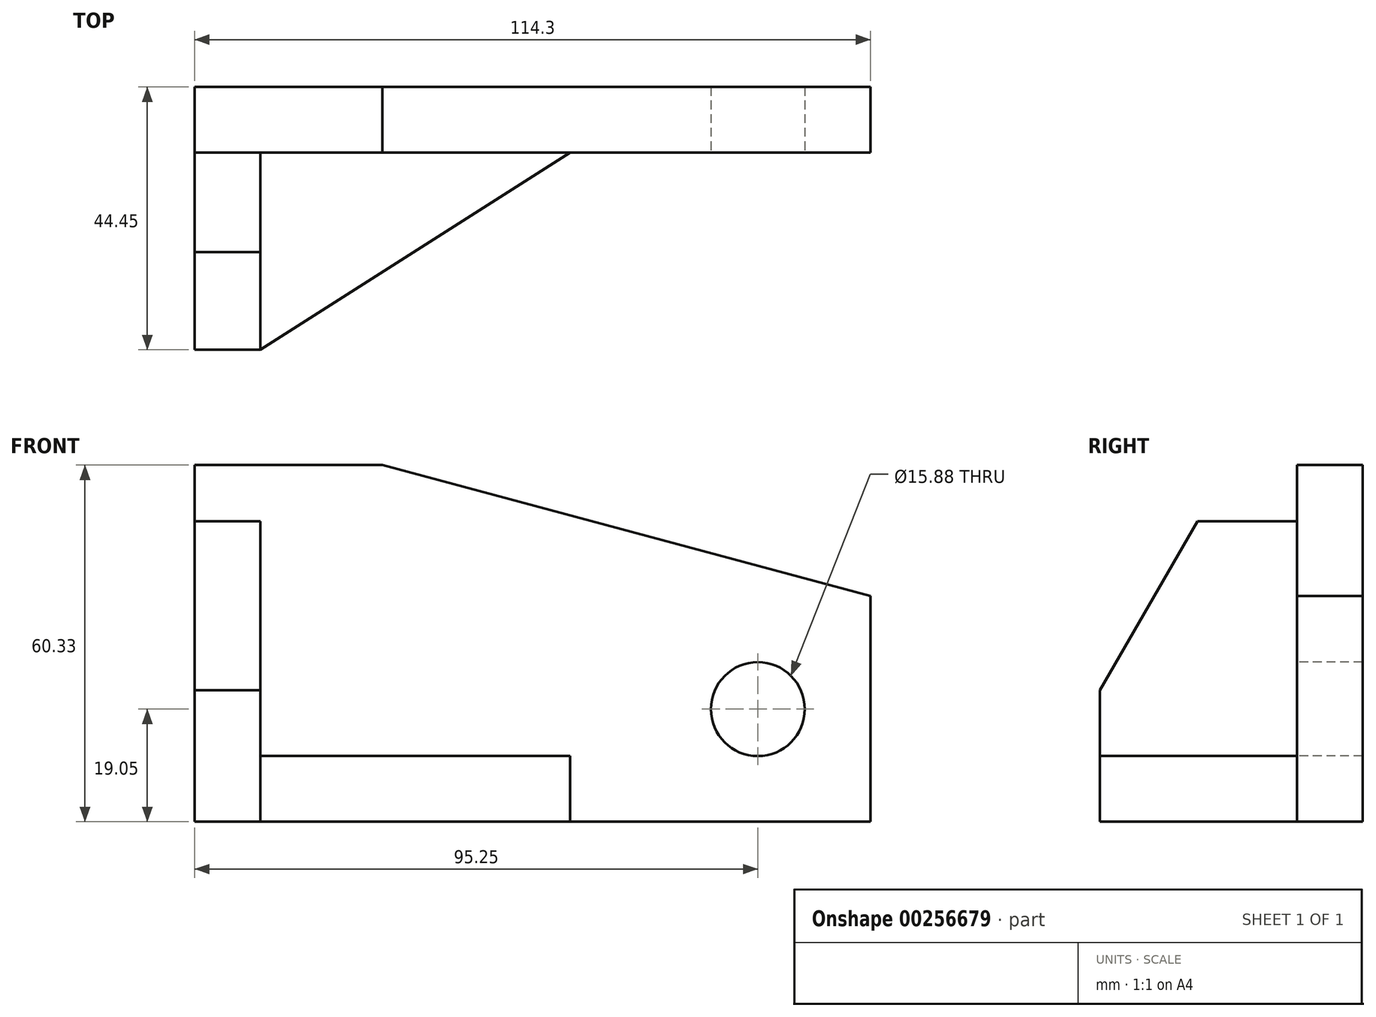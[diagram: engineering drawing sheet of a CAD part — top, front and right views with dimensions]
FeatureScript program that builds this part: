
annotation { "Feature Type Name" : "Feature", "Feature Type Description" : "" }
export const myFeature = defineFeature(function(context is Context, id is Id, definition is map)
    precondition{}
    {
        {
            var Q0;
            Q0=qCreatedBy(makeId("Top.planeOp"),FACE);
            var sketch = newSketch(context, id + "F0", { "sketchPlane" : qUnion([Q0])});
            skLineSegment(sketch, "E0", {"start": v(0, 0) * mm, "end": v(114.3, 0) * mm});
            skLineSegment(sketch, "E1", {"start": v(114.3, 0) * mm, "end": v(114.3, -11.11) * mm});
            skLineSegment(sketch, "E2", {"start": v(0, 0) * mm, "end": v(0, -44.45) * mm});
            skLineSegment(sketch, "E3", {"start": v(0, -44.45) * mm, "end": v(11.11, -44.45) * mm});
            skLineSegment(sketch, "E4", {"start": v(11.11, -44.45) * mm, "end": v(11.11, -11.11) * mm});
            skLineSegment(sketch, "E5", {"start": v(11.11, -11.11) * mm, "end": v(114.3, -11.11) * mm});
            skLineSegment(sketch, "E6", {"start": v(11.11, -44.45) * mm, "end": v(63.5, -11.11) * mm});
            skLineSegment(sketch, "E7", {"start": v(11.11, -11.11) * mm, "end": v(0, -11.11) * mm});
            skLineSegment(sketch, "E8", {"start": v(11.11, -44.45) * mm, "end": v(0, -44.45) * mm});
            skSolve(sketch);
        }
        {
            var Q0;
            {var subQ4=sQuery(id+"F0.wireOp",EDGE,"E0");Q0=makeQuery(id+"F0.imprint","IMPRINT",FACE,{"disambiguationData":[TD([[makeQuery(id+"F0.imprint","IMPRINT",EDGE,{"derivedFrom":subQ4}),-1.0]])]});}
            extrude(context, id + "F1", {"entities" : qUnion([Q0]), "depth" : 60.32 * mm});
        }
        {
            var Q0;
            {var subQ0=sQuery(id+"F0.wireOp",EDGE,"E4");Q0=makeQuery(id+"F0.imprint","IMPRINT",FACE,{"disambiguationData":[TD([[makeQuery(id+"F0.imprint","IMPRINT",EDGE,{"derivedFrom":subQ0}),-1.0]])]});}
            extrude(context, id + "F2", {"entities" : qUnion([Q0]), "operationType" : NewBodyOperationType.ADD, "depth" : 11.1 * mm});
        }
        {
            var Q0;
            Q0=makeQuery(id+"F1.opExtrude","SWEPT_FACE",FACE,{"disambiguationData":[OSD([sQuery(id+"F0.wireOp",EDGE,"E5"),sQuery(id+"F0.wireOp",EDGE,"E7")])]});
            var sketch = newSketch(context, id + "F3", { "sketchPlane" : qUnion([Q0])});
            skLineSegment(sketch, "E9", {"start": v(0, 60.33) * mm, "end": v(31.75, 60.33) * mm});
            skLineSegment(sketch, "E10", {"start": v(31.75, 60.33) * mm, "end": v(114.3, 38.2) * mm});
            skLineSegment(sketch, "E11", {"start": v(114.3, 0) * mm, "end": v(95.25, 0) * mm});
            skLineSegment(sketch, "E12", {"start": v(95.25, 0) * mm, "end": v(95.25, 19.05) * mm});
            skCircle(sketch, "E13", {"center": v(95.25, 19.05) * mm, "radius": 7.94 * mm});
            skSolve(sketch);
        }
        {
            var Q0;
            {var subQ0=sQuery(id+"F3.wireOp",EDGE,"E10");Q0=makeQuery(id+"F3.imprint","IMPRINT",FACE,{"disambiguationData":[TD([[makeQuery(id+"F3.imprint","IMPRINT",EDGE,{"derivedFrom":subQ0}),1.0]])]});}
            extrude(context, id + "F4", {"entities" : qUnion([Q0]), "operationType" : NewBodyOperationType.REMOVE, "oppositeDirection" : true, "depth" : 11.1 * mm});
        }
        {
            var Q0;
            Q0=makeQuery(id+"F0.imprint","IMPRINT",FACE,{"disambiguationData":[TD([[makeQuery(id+"F0.imprint","IMPRINT",EDGE,{"derivedFrom":sQuery(id+"F0.wireOp",EDGE,"E4")}),1.0]])]});
            extrude(context, id + "F5", {"entities" : qUnion([Q0]), "operationType" : NewBodyOperationType.ADD, "depth" : 50.8 * mm});
        }
        {
            var Q0;
            Q0=makeQuery(id+"F3.imprint","IMPRINT",FACE,{"disambiguationData":[TD([[makeQuery(id+"F3.imprint","IMPRINT",EDGE,{"derivedFrom":sQuery(id+"F3.wireOp",EDGE,"E13")}),1.0]])]});
            extrude(context, id + "F6", {"entities" : qUnion([Q0]), "operationType" : NewBodyOperationType.REMOVE, "oppositeDirection" : true, "depth" : 25.4 * mm});
        }
        {
            var Q0;
            Q0=makeQuery(id+"F5.opExtrude","SWEPT_FACE",FACE,{"disambiguationData":[OSD([sQuery(id+"F0.wireOp",EDGE,"E4")])]});
            var sketch = newSketch(context, id + "F7", { "sketchPlane" : qUnion([Q0])});
            skLineSegment(sketch, "E14", {"start": v(-44.45, 0) * mm, "end": v(-44.45, 22.23) * mm});
            skLineSegment(sketch, "E15", {"start": v(-44.45, 22.23) * mm, "end": v(-27.74, 51.17) * mm});
            skPoint(sketch, "E16", {"position": v(-27.78, 50.8) * mm});
            skSolve(sketch);
        }
        {
            var Q0;
            {var subQ0=sQuery(id+"F7.wireOp",EDGE,"E15");var subQ1=sQuery(id+"F0.wireOp",EDGE,"E4");var subQ4=makeQuery(id+"F5.opExtrude","CAP_EDGE",EDGE,{"disambiguationData":[OSD([subQ1])],"isStart":false});var subQ5=makeQuery(id+"F7.imprint","INTERSECT",VERTEX,{"derivedFrom":[subQ4,subQ0]});Q0=makeQuery(id+"F7.imprint","IMPRINT",FACE,{"disambiguationData":[TD([[makeQuery(id+"F7.imprint","IMPRINT",EDGE,{"disambiguationData":[TD([[subQ5,1.0]])],"derivedFrom":subQ4}),-1.0]])]});}
            extrude(context, id + "F8", {"entities" : qUnion([Q0]), "operationType" : NewBodyOperationType.REMOVE, "oppositeDirection" : true, "depth" : 11.1 * mm});
        }
    });
